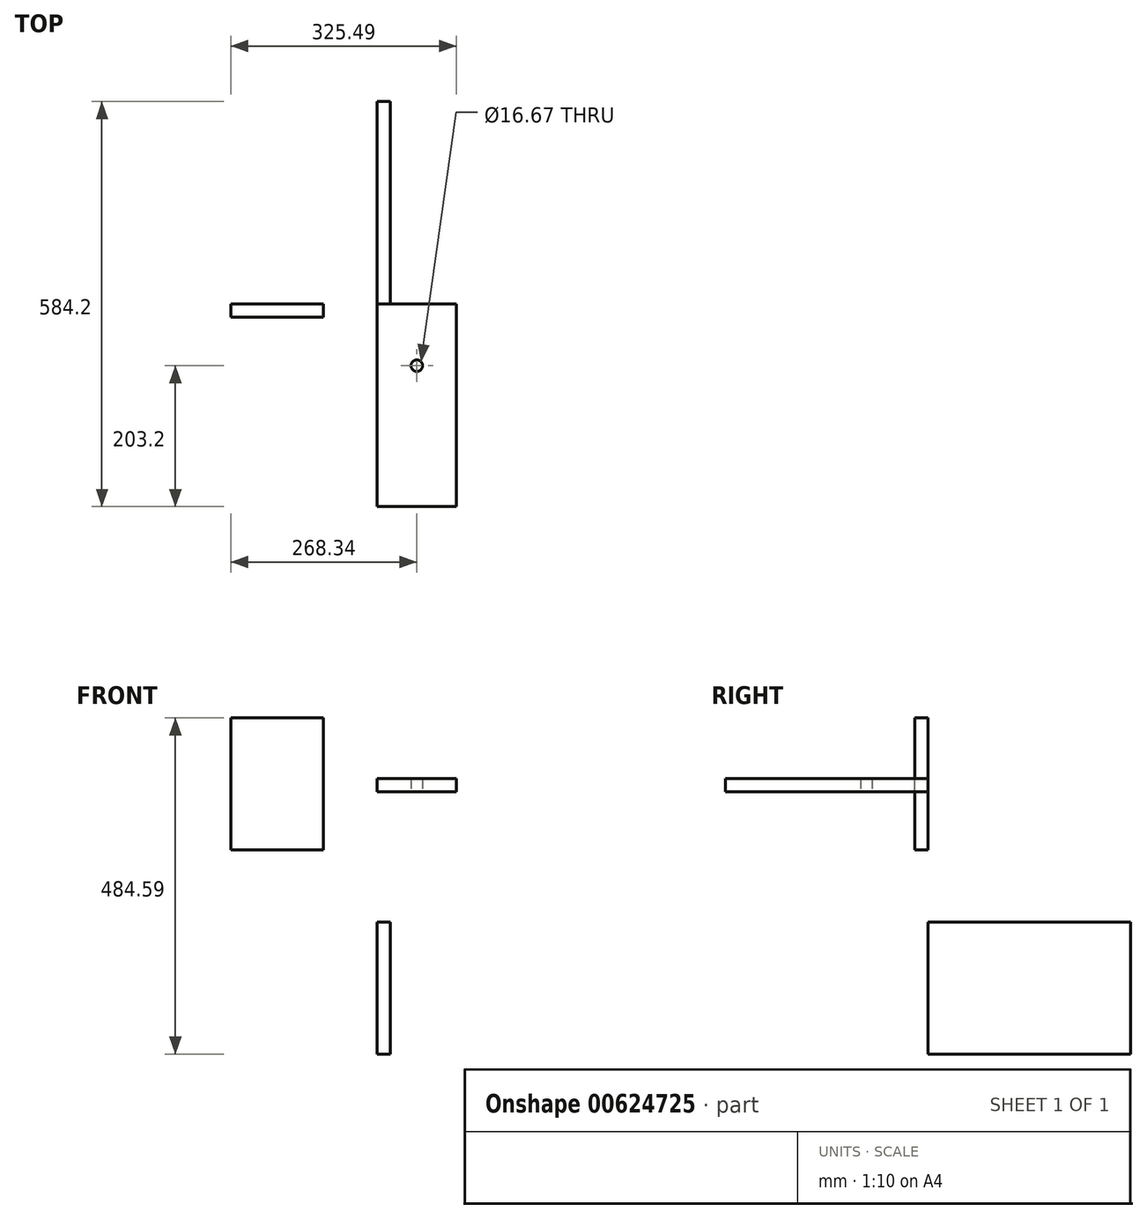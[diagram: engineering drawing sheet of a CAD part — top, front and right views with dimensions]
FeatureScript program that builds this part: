
annotation { "Feature Type Name" : "Feature", "Feature Type Description" : "" }
export const myFeature = defineFeature(function(context is Context, id is Id, definition is map)
    precondition{}
    {
        {
            var Q0;
            Q0=qCreatedBy(makeId("Top.planeOp"),FACE);
            var sketch = newSketch(context, id + "F0", { "sketchPlane" : qUnion([Q0])});
            skLineSegment(sketch, "E0.bottom", {"start": v(0, 0) * mm, "end": v(114.3, 0) * mm});
            skLineSegment(sketch, "E0.top", {"start": v(0, -292.1) * mm, "end": v(114.3, -292.1) * mm});
            skLineSegment(sketch, "E0.left", {"start": v(0, 0) * mm, "end": v(0, -292.1) * mm});
            skLineSegment(sketch, "E0.right", {"start": v(114.3, 0) * mm, "end": v(114.3, -292.1) * mm});
            skCircle(sketch, "E1", {"center": v(57.15, -88.9) * mm, "radius": 8.33 * mm});
            skSolve(sketch);
        }
        {
            var Q0;
            Q0=makeQuery(id+"F0.imprint","IMPRINT",FACE,{"disambiguationData":[TD([[makeQuery(id+"F0.imprint","IMPRINT",EDGE,{"derivedFrom":sQuery(id+"F0.wireOp",EDGE,"E0.bottom")}),-1.0]])]});
            extrude(context, id + "F1", {"entities" : qUnion([Q0]), "depth" : 19.05 * mm, "offsetDistance" : 25.4 * mm});
        }
        {
            var Q0;
            Q0=qCreatedBy(makeId("Right.planeOp"),FACE);
            var sketch = newSketch(context, id + "F2", { "sketchPlane" : qUnion([Q0])});
            skLineSegment(sketch, "E2.bottom", {"start": v(292.1, -187.97) * mm, "end": v(0, -187.97) * mm});
            skLineSegment(sketch, "E2.top", {"start": v(292.1, -378.47) * mm, "end": v(0, -378.47) * mm});
            skLineSegment(sketch, "E2.left", {"start": v(292.1, -187.97) * mm, "end": v(292.1, -378.47) * mm});
            skLineSegment(sketch, "E2.right", {"start": v(0, -187.97) * mm, "end": v(0, -378.47) * mm});
            skSolve(sketch);
        }
        {
            var Q0;
            Q0=makeQuery(id+"F2.imprint","IMPRINT",FACE,{"disambiguationData":[TD([[makeQuery(id+"F2.imprint","IMPRINT",EDGE,{"derivedFrom":sQuery(id+"F2.wireOp",EDGE,"E2.bottom")}),1.0]])]});
            extrude(context, id + "F3", {"entities" : qUnion([Q0]), "depth" : 19.05 * mm, "offsetDistance" : 25.4 * mm});
        }
        {
            var Q0;
            Q0=qCreatedBy(makeId("Front.planeOp"),FACE);
            var sketch = newSketch(context, id + "F4", { "sketchPlane" : qUnion([Q0])});
            skLineSegment(sketch, "E3.bottom", {"start": v(-211.19, -84.38) * mm, "end": v(-77.84, -84.38) * mm});
            skLineSegment(sketch, "E3.top", {"start": v(-211.19, 106.12) * mm, "end": v(-77.84, 106.12) * mm});
            skLineSegment(sketch, "E3.left", {"start": v(-211.19, -84.38) * mm, "end": v(-211.19, 106.12) * mm});
            skLineSegment(sketch, "E3.right", {"start": v(-77.84, -84.38) * mm, "end": v(-77.84, 106.12) * mm});
            skSolve(sketch);
        }
        {
            var Q0;
            Q0=makeQuery(id+"F4.imprint","IMPRINT",FACE,{"disambiguationData":[TD([[makeQuery(id+"F4.imprint","IMPRINT",EDGE,{"derivedFrom":sQuery(id+"F4.wireOp",EDGE,"E3.bottom")}),1.0]])]});
            extrude(context, id + "F5", {"entities" : qUnion([Q0]), "depth" : 19.05 * mm, "offsetDistance" : 25.4 * mm});
        }
    });
